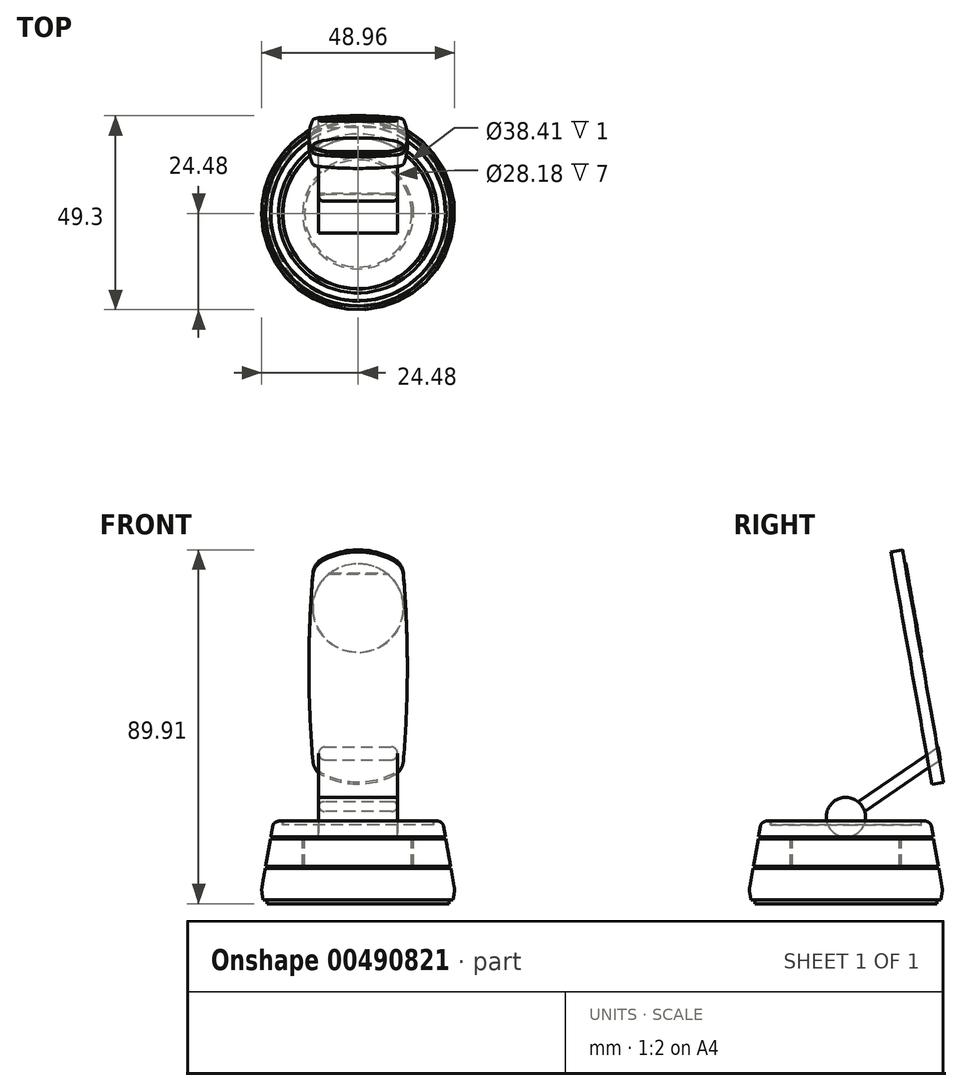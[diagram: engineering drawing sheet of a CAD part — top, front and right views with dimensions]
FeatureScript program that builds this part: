
annotation { "Feature Type Name" : "Feature", "Feature Type Description" : "" }
export const myFeature = defineFeature(function(context is Context, id is Id, definition is map)
    precondition{}
    {
        {
            var Q0;
            Q0=qCreatedBy(makeId("Right.planeOp"),FACE);
            var sketch = newSketch(context, id + "F0", { "sketchPlane" : qUnion([Q0])});
            skLineSegment(sketch, "E0", {"start": v(0, 0) * mm, "end": v(25, 0) * mm});
            skLineSegment(sketch, "E1", {"start": v(25, 0) * mm, "end": v(23.59, 8) * mm});
            skLineSegment(sketch, "E2", {"start": v(23.59, 8) * mm, "end": v(13.59, 8) * mm});
            skLineSegment(sketch, "E3", {"start": v(13.59, 8) * mm, "end": v(13.59, 16) * mm});
            skLineSegment(sketch, "E4", {"start": v(13.59, 16) * mm, "end": v(22.18, 16) * mm});
            skLineSegment(sketch, "E5", {"start": v(22.18, 16) * mm, "end": v(21.47, 20) * mm});
            skLineSegment(sketch, "E6", {"start": v(21.47, 20) * mm, "end": v(0, 20) * mm});
            skLineSegment(sketch, "E7", {"start": v(0, 20) * mm, "end": v(0, 0) * mm});
            skLineSegment(sketch, "E8", {"start": v(21.47, 20) * mm, "end": v(25, 0) * mm, "construction": true});
            skLineSegment(sketch, "E9", {"start": v(22.27, 15.5) * mm, "end": v(14.09, 15.5) * mm});
            skLineSegment(sketch, "E10", {"start": v(14.09, 15.5) * mm, "end": v(14.09, 8.5) * mm});
            skLineSegment(sketch, "E11", {"start": v(14.09, 8.5) * mm, "end": v(23.5, 8.5) * mm});
            skLineSegment(sketch, "E12", {"start": v(23.5, 8.5) * mm, "end": v(22.27, 15.5) * mm});
            skLineSegment(sketch, "E13", {"start": v(22.45, 26) * mm, "end": v(12.03, 85.09) * mm, "construction": true});
            skLineSegment(sketch, "E14", {"start": v(22.45, 26) * mm, "end": v(22.45, 40.65) * mm, "construction": true});
            skSolve(sketch);
        }
        {
            var Q0;
            Q0=makeQuery(id+"F0.imprint","IMPRINT",FACE,{"disambiguationData":[TD([[makeQuery(id+"F0.imprint","IMPRINT",EDGE,{"derivedFrom":sQuery(id+"F0.wireOp",EDGE,"E0")}),1.0]])]});
            var Q1;
            Q1=makeQuery(id+"F0.imprint","IMPRINT",FACE,{"disambiguationData":[TD([[makeQuery(id+"F0.imprint","IMPRINT",EDGE,{"derivedFrom":sQuery(id+"F0.wireOp",EDGE,"E9")}),1.0]])]});
            var Q2;
            Q2=sQuery(id+"F0.wireOp",EDGE,"E7");
            revolve(context, id + "F1", {"entities" : qUnion([Q0, Q1]), "axis" : qUnion([Q2]), "revolveType" : RevolveType.FULL});
        }
        {
            var Q0;
            Q0=makeQuery(id+"F1.opRevolve","SWEPT_EDGE",EDGE,{"disambiguationData":[OSD([sQuery(id+"F0.wireOp",EDGE,"E0"),sQuery(id+"F0.wireOp",EDGE,"E1")])]});
            chamfer(context, id + "F2", {"entities" : qUnion([Q0]), "chamferType" : ChamferType.OFFSET_ANGLE, "width" : 2.54 * mm, "oppositeDirection" : false, "angle" : 20 * degree, "tangentPropagation" : true});
        }
        {
            var Q0;
            Q0=makeQuery(id+"F1.opRevolve","SWEPT_EDGE",EDGE,{"disambiguationData":[OSD([sQuery(id+"F0.wireOp",EDGE,"E5"),sQuery(id+"F0.wireOp",EDGE,"E6")])]});
            chamfer(context, id + "F3", {"entities" : qUnion([Q0]), "chamferType" : ChamferType.OFFSET_ANGLE, "width" : 1.27 * mm, "oppositeDirection" : false, "angle" : 20 * degree, "tangentPropagation" : true});
        }
        {
            var Q0;
            {var subQ0=sQuery(id+"F0.wireOp",EDGE,"E5");Q0=makeQuery(id+"F3.opChamfer","BLEND_EDGE",EDGE,{"blendedFrom":[makeQuery(id+"F1.opRevolve","SWEPT_EDGE",EDGE,{"disambiguationData":[OSD([subQ0,sQuery(id+"F0.wireOp",EDGE,"E6")])]}),makeQuery(id+"F1.opRevolve","SWEPT_FACE",FACE,{"disambiguationData":[OSD([subQ0])]})],"blendedInto":[makeQuery(id+"F1.opRevolve","SWEPT_FACE",FACE,{"disambiguationData":[OSD([subQ0])]})]});}
            fillet(context, id + "F4", {"entities" : qUnion([Q0]), "radius" : 1.27 * mm, "tangentPropagation" : true, "allowEdgeOverflow" : false});
        }
        {
            var Q0;
            {var subQ0=sQuery(id+"F0.wireOp",EDGE,"E1");Q0=makeQuery(id+"F2.opChamfer","BLEND_EDGE",EDGE,{"blendedFrom":[makeQuery(id+"F1.opRevolve","SWEPT_EDGE",EDGE,{"disambiguationData":[OSD([sQuery(id+"F0.wireOp",EDGE,"E0"),subQ0])]}),makeQuery(id+"F1.opRevolve","SWEPT_FACE",FACE,{"disambiguationData":[OSD([subQ0])]})],"blendedInto":[makeQuery(id+"F1.opRevolve","SWEPT_FACE",FACE,{"disambiguationData":[OSD([subQ0])]})]});}
            fillet(context, id + "F5", {"entities" : qUnion([Q0]), "radius" : 5.08 * mm, "tangentPropagation" : true, "allowEdgeOverflow" : false});
        }
        {
            var Q0;
            Q0=makeQuery(id+"F1.opRevolve","SWEPT_FACE",FACE,{"disambiguationData":[OSD([sQuery(id+"F0.wireOp",EDGE,"E0")])]});
            var sketch = newSketch(context, id + "F6", { "sketchPlane" : qUnion([Q0])});
            skCircle(sketch, "E15.0", {"center": v(0, 0) * mm, "radius": 23.12 * mm});
            skSolve(sketch);
        }
        {
            var Q0;
            Q0 = qSketchRegion(id + "F6", true);
            extrude(context, id + "F7", {"entities" : qUnion([Q0]), "depth" : 1 * mm});
        }
        {
            var Q0;
            Q0=makeQuery(id+"F1.opRevolve","SWEPT_FACE",FACE,{"disambiguationData":[OSD([sQuery(id+"F0.wireOp",EDGE,"E6")])]});
            var sketch = newSketch(context, id + "F8", { "sketchPlane" : qUnion([Q0])});
            skCircle(sketch, "E16.0", {"center": v(0, 0) * mm, "radius": 19.2 * mm});
            skSolve(sketch);
        }
        {
            var Q0;
            Q0 = qSketchRegion(id + "F8", true);
            extrude(context, id + "F9", {"entities" : qUnion([Q0]), "operationType" : NewBodyOperationType.REMOVE, "oppositeDirection" : true, "depth" : 1 * mm});
        }
        {
            var Q0;
            Q0=makeQuery(id+"F9.boolean.opBoolean","COPY",FACE,{"derivedFrom":makeQuery(id+"F9.opExtrude","CAP_FACE",FACE,{"disambiguationData":[OSD([sQuery(id+"F8.wireOp",EDGE,"E16.0")])],"isStart":false})});
            var sketch = newSketch(context, id + "F10", { "sketchPlane" : qUnion([Q0])});
            skCircle(sketch, "E17.0", {"center": v(0, 0) * mm, "radius": 19.1 * mm});
            skSolve(sketch);
        }
        {
            var Q0;
            Q0 = qSketchRegion(id + "F10", true);
            extrude(context, id + "F11", {"entities" : qUnion([Q0]), "depth" : 1 * mm});
        }
        {
            var Q0;
            Q0=qCreatedBy(makeId("Right.planeOp"),FACE);
            var sketch = newSketch(context, id + "F12", { "sketchPlane" : qUnion([Q0])});
            skLineSegment(sketch, "E18.0", {"start": v(21.86, 29.3) * mm, "end": v(11.44, 88.4) * mm});
            skSolve(sketch);
        }
        {
            var Q0;
            Q0 = qSketchRegion(id + "F12", true);
            var Q1;
            Q1=sQuery(id+"F12.wireOp",EDGE,"E18.0");
            extrude(context, id + "F13", {"entities" : qUnion([Q0]), "bodyType" : ToolBodyType.SURFACE, "surfaceEntities" : qUnion([Q1]), "endBound" : BoundingType.SYMMETRIC, "depth" : 25 * mm});
        }
        {
            var Q0;
            Q0=makeQuery(id+"F13.opExtrude","SWEPT_FACE",FACE,{"disambiguationData":[OSD([sQuery(id+"F12.wireOp",EDGE,"E18.0")])]});
            var sketch = newSketch(context, id + "F14", { "sketchPlane" : qUnion([Q0])});
            skLineSegment(sketch, "E19", {"start": v(0, 85.06) * mm, "end": v(0, 25.06) * mm, "construction": true});
            skLineSegment(sketch, "E20", {"start": v(0, 79.06) * mm, "end": v(-11.5, 79.06) * mm, "construction": true});
            skLineSegment(sketch, "E21", {"start": v(-11.5, 79.06) * mm, "end": v(-11.5, 31.06) * mm, "construction": true});
            skLineSegment(sketch, "E22", {"start": v(-11.5, 31.06) * mm, "end": v(0, 31.06) * mm, "construction": true});
            skLineSegment(sketch, "E23", {"start": v(0, 31.06) * mm, "end": v(11.5, 31.06) * mm, "construction": true});
            skLineSegment(sketch, "E24", {"start": v(11.5, 31.06) * mm, "end": v(11.5, 79.06) * mm, "construction": true});
            skLineSegment(sketch, "E25", {"start": v(11.5, 79.06) * mm, "end": v(0, 79.06) * mm, "construction": true});
            skArc(sketch, "E26", {"start": v(-11.5, 79.06) * mm, "mid": v(-12.5, 55.06) * mm, "end": v(-11.5, 31.06) * mm});
            skArc(sketch, "E27", {"start": v(11.5, 31.06) * mm, "mid": v(12.5, 55.06) * mm, "end": v(11.5, 79.06) * mm});
            skArc(sketch, "E28", {"start": v(-9.14, 82.7) * mm, "mid": v(-10.78, 81.18) * mm, "end": v(-11.5, 79.06) * mm});
            skArc(sketch, "E29", {"start": v(11.5, 79.06) * mm, "mid": v(10.78, 81.18) * mm, "end": v(9.14, 82.7) * mm});
            skArc(sketch, "E30", {"start": v(9.14, 82.7) * mm, "mid": v(0, 85.06) * mm, "end": v(-9.14, 82.7) * mm});
            skArc(sketch, "E31", {"start": v(-11.5, 31.06) * mm, "mid": v(-10.78, 28.95) * mm, "end": v(-9.14, 27.42) * mm});
            skArc(sketch, "E32", {"start": v(9.14, 27.42) * mm, "mid": v(10.78, 28.95) * mm, "end": v(11.5, 31.06) * mm});
            skArc(sketch, "E33", {"start": v(-9.14, 27.42) * mm, "mid": v(0, 25.06) * mm, "end": v(9.14, 27.42) * mm});
            skLineSegment(sketch, "E34", {"start": v(-9.14, 27.42) * mm, "end": v(-9.14, 82.7) * mm, "construction": true});
            skLineSegment(sketch, "E35", {"start": v(9.14, 82.7) * mm, "end": v(9.14, 27.42) * mm, "construction": true});
            skLineSegment(sketch, "E36", {"start": v(-9.14, 82.7) * mm, "end": v(9.14, 82.7) * mm, "construction": true});
            skLineSegment(sketch, "E37", {"start": v(0, 85.06) * mm, "end": v(0, 85.06) * mm});
            skSolve(sketch);
        }
        {
            var Q0;
            Q0 = qSketchRegion(id + "F14", true);
            extrude(context, id + "F15", {"entities" : qUnion([Q0]), "depth" : 3 * mm});
        }
        {
            var Q0;
            Q0=makeQuery(id+"F15.opExtrude","CAP_FACE",FACE,{"disambiguationData":[OSD([sQuery(id+"F14.wireOp",EDGE,"E26"),sQuery(id+"F14.wireOp",EDGE,"E27"),sQuery(id+"F14.wireOp",EDGE,"E28"),sQuery(id+"F14.wireOp",EDGE,"E29"),sQuery(id+"F14.wireOp",EDGE,"E30"),sQuery(id+"F14.wireOp",EDGE,"E31"),sQuery(id+"F14.wireOp",EDGE,"E32"),sQuery(id+"F14.wireOp",EDGE,"E33")])],"isStart":false});
            var sketch = newSketch(context, id + "F16", { "sketchPlane" : qUnion([Q0])});
            skLineSegment(sketch, "E38", {"start": v(0, 85.06) * mm, "end": v(0, 70.06) * mm, "construction": true});
            skPoint(sketch, "E38.endSnap0", {"position": v(0, 85.06) * mm});
            skCircle(sketch, "E39", {"center": v(0, 70.06) * mm, "radius": 12 * mm, "construction": true});
            skCircle(sketch, "E40.0", {"center": v(0, 70.06) * mm, "radius": 11.5 * mm});
            skSolve(sketch);
        }
        {
            var Q0;
            Q0=makeQuery(id+"F16.imprint","IMPRINT",FACE,{"disambiguationData":[TD([[makeQuery(id+"F16.imprint","IMPRINT",EDGE,{"derivedFrom":sQuery(id+"F16.wireOp",EDGE,"E40.0")}),1.0]])]});
            var Q1;
            Q1=sQuery(id+"F16.wireOp",EDGE,"E39");
            extrude(context, id + "F17", {"entities" : qUnion([Q0]), "surfaceEntities" : qUnion([Q1]), "depth" : .245 * mm});
        }
        {
            var Q0;
            Q0=qCreatedBy(makeId("Right.planeOp"),FACE);
            var sketch = newSketch(context, id + "F18", { "sketchPlane" : qUnion([Q0])});
            skCircle(sketch, "E41", {"center": v(0, 21) * mm, "radius": 5 * mm});
            skLineSegment(sketch, "E42", {"start": v(0, 21) * mm, "end": v(0, 20) * mm, "construction": true});
            skLineSegment(sketch, "E43", {"start": v(0, 21) * mm, "end": v(25.13, 38.17) * mm, "construction": true});
            skLineSegment(sketch, "E44.0", {"start": v(-1.4, 18.23) * mm, "end": v(25.9, 36.89) * mm});
            skLineSegment(sketch, "E45.0", {"start": v(-2.96, 20.8) * mm, "end": v(24.34, 39.45) * mm});
            skLineSegment(sketch, "E46", {"start": v(-2.96, 20.8) * mm, "end": v(-1.4, 18.23) * mm});
            skLineSegment(sketch, "E47", {"start": v(24.34, 39.45) * mm, "end": v(25.9, 36.89) * mm});
            skSolve(sketch);
        }
        {
            var Q0;
            Q0 = qSketchRegion(id + "F18", true);
            extrude(context, id + "F19", {"entities" : qUnion([Q0]), "endBound" : BoundingType.SYMMETRIC, "depth" : 20 * mm});
        }
        {
            var Q0;
            Q0=makeQuery(id+"F19.opExtrude","CAP_EDGE",EDGE,{"disambiguationData":[OSD([sQuery(id+"F18.wireOp",EDGE,"E44.0")])],"isStart":false});
            var Q1;
            Q1=makeQuery(id+"F19.opExtrude","CAP_EDGE",EDGE,{"disambiguationData":[OSD([sQuery(id+"F18.wireOp",EDGE,"E45.0")])],"isStart":false});
            var Q2;
            Q2=makeQuery(id+"F19.opExtrude","CAP_EDGE",EDGE,{"disambiguationData":[OSD([sQuery(id+"F18.wireOp",EDGE,"E44.0")])],"isStart":true});
            var Q3;
            Q3=makeQuery(id+"F19.opExtrude","CAP_EDGE",EDGE,{"disambiguationData":[OSD([sQuery(id+"F18.wireOp",EDGE,"E45.0")])],"isStart":true});
            fillet(context, id + "F20", {"entities" : qUnion([Q0, Q1, Q2, Q3]), "radius" : 1.5 * mm, "tangentPropagation" : true, "allowEdgeOverflow" : false});
        }
        {
            var Q0;
            Q0=qCreatedBy(makeId("Right.planeOp"),FACE);
            var sketch = newSketch(context, id + "F21", { "sketchPlane" : qUnion([Q0])});
            skLineSegment(sketch, "E48.0", {"start": v(23.97, 35.77) * mm, "end": v(24.6, 32.18) * mm});
            skLineSegment(sketch, "E48.1", {"start": v(15.64, 83.04) * mm, "end": v(23.97, 35.77) * mm});
            skLineSegment(sketch, "E49", {"start": v(24.6, 32.18) * mm, "end": v(30.9, 39.7) * mm});
            skLineSegment(sketch, "E50", {"start": v(30.9, 39.7) * mm, "end": v(15.64, 83.04) * mm});
            skSolve(sketch);
        }
        {
            var Q0;
            Q0 = qSketchRegion(id + "F21", true);
            extrude(context, id + "F22", {"entities" : qUnion([Q0]), "operationType" : NewBodyOperationType.REMOVE, "endBound" : BoundingType.SYMMETRIC, "oppositeDirection" : true, "depth" : 60 * mm});
        }
    });
